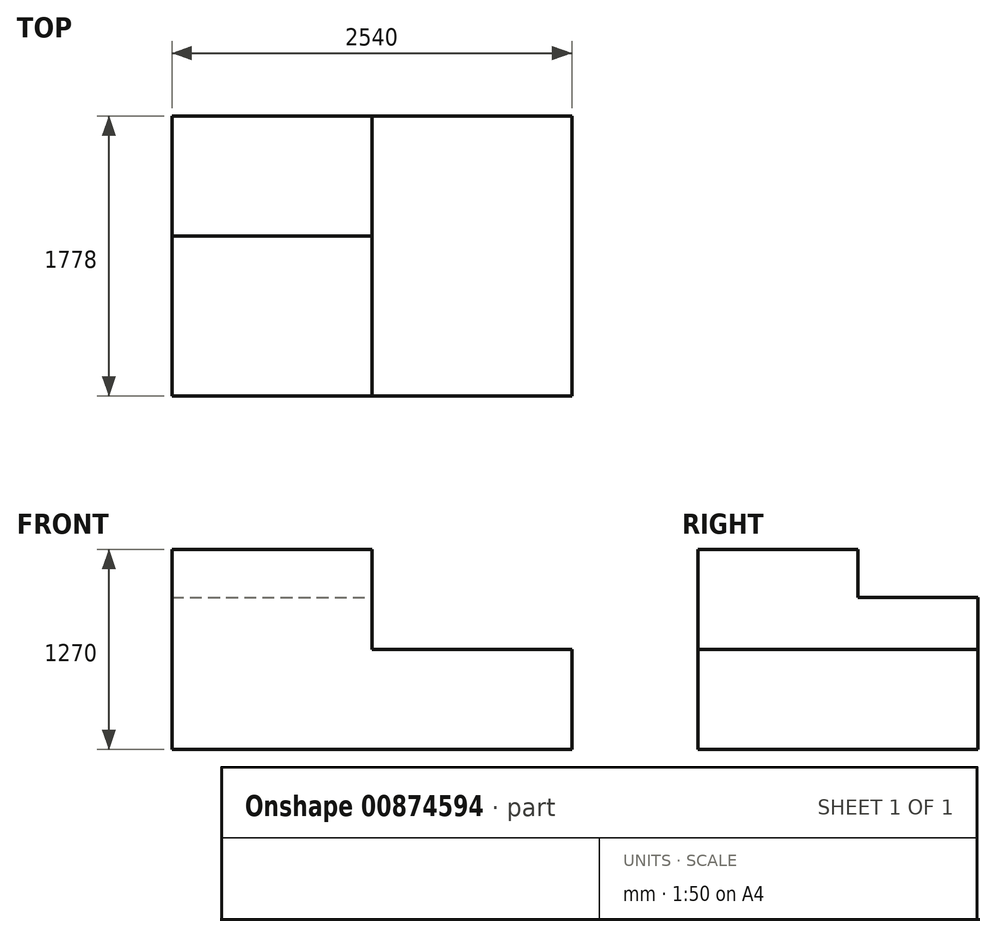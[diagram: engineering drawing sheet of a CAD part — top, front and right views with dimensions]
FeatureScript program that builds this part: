
annotation { "Feature Type Name" : "Feature", "Feature Type Description" : "" }
export const myFeature = defineFeature(function(context is Context, id is Id, definition is map)
    precondition{}
    {
        {
            var Q0;
            Q0=qCreatedBy(makeId("Top.planeOp"),FACE);
            var sketch = newSketch(context, id + "F0", { "sketchPlane" : qUnion([Q0])});
            skLineSegment(sketch, "E0.bottom", {"start": v(-1270, 889) * mm, "end": v(1270, 889) * mm});
            skLineSegment(sketch, "E0.top", {"start": v(-1270, -889) * mm, "end": v(1270, -889) * mm});
            skLineSegment(sketch, "E0.left", {"start": v(-1270, 889) * mm, "end": v(-1270, -889) * mm});
            skLineSegment(sketch, "E0.right", {"start": v(1270, 889) * mm, "end": v(1270, -889) * mm});
            skPoint(sketch, "E0.middle", {"position": v(0, 0) * mm});
            skSolve(sketch);
        }
        {
            var Q0;
            Q0=makeQuery(id+"F0.imprint","IMPRINT",FACE,{"disambiguationData":[TD([[makeQuery(id+"F0.imprint","IMPRINT",EDGE,{"derivedFrom":sQuery(id+"F0.wireOp",EDGE,"E0.bottom")}),-1.0]])]});
            extrude(context, id + "F1", {"entities" : qUnion([Q0]), "depth" : 1270 * mm, "offsetDistance" : 25.4 * mm});
        }
        {
            var Q0;
            Q0=makeQuery(id+"F1.opExtrude","SWEPT_FACE",FACE,{"disambiguationData":[OSD([sQuery(id+"F0.wireOp",EDGE,"E0.top")])]});
            var sketch = newSketch(context, id + "F2", { "sketchPlane" : qUnion([Q0])});
            skLineSegment(sketch, "E1", {"start": v(1270, 635) * mm, "end": v(0, 635) * mm});
            skLineSegment(sketch, "E2", {"start": v(0, 635) * mm, "end": v(0, 1270) * mm});
            skSolve(sketch);
        }
        {
            var Q0;
            {var subQ0=sQuery(id+"F2.wireOp",EDGE,"E1");Q0=makeQuery(id+"F2.imprint","IMPRINT",FACE,{"disambiguationData":[TD([[makeQuery(id+"F2.imprint","IMPRINT",EDGE,{"derivedFrom":subQ0}),-1.0]])]});}
            extrude(context, id + "F3", {"entities" : qUnion([Q0]), "operationType" : NewBodyOperationType.REMOVE, "oppositeDirection" : true, "depth" : 3934.46 * mm, "offsetDistance" : 25.4 * mm});
        }
        {
            var Q0;
            Q0=makeQuery(id+"F3.boolean.opBoolean","COPY",FACE,{"derivedFrom":makeQuery(id+"F3.opExtrude","SWEPT_FACE",FACE,{"disambiguationData":[OSD([sQuery(id+"F2.wireOp",EDGE,"E2")])]})});
            var sketch = newSketch(context, id + "F4", { "sketchPlane" : qUnion([Q0])});
            skLineSegment(sketch, "E3", {"start": v(-889, 1270) * mm, "end": v(127, 1270) * mm});
            skLineSegment(sketch, "E4", {"start": v(127, 1270) * mm, "end": v(127, 965.2) * mm});
            skLineSegment(sketch, "E5", {"start": v(127, 965.2) * mm, "end": v(889, 965.2) * mm});
            skSolve(sketch);
        }
        {
            var Q0;
            {var subQ0=sQuery(id+"F4.wireOp",EDGE,"E4");Q0=makeQuery(id+"F4.imprint","IMPRINT",FACE,{"disambiguationData":[TD([[makeQuery(id+"F4.imprint","IMPRINT",EDGE,{"derivedFrom":subQ0}),1.0]])]});}
            extrude(context, id + "F5", {"entities" : qUnion([Q0]), "operationType" : NewBodyOperationType.REMOVE, "oppositeDirection" : true, "depth" : 1610.36 * mm, "offsetDistance" : 25.4 * mm});
        }
    });
